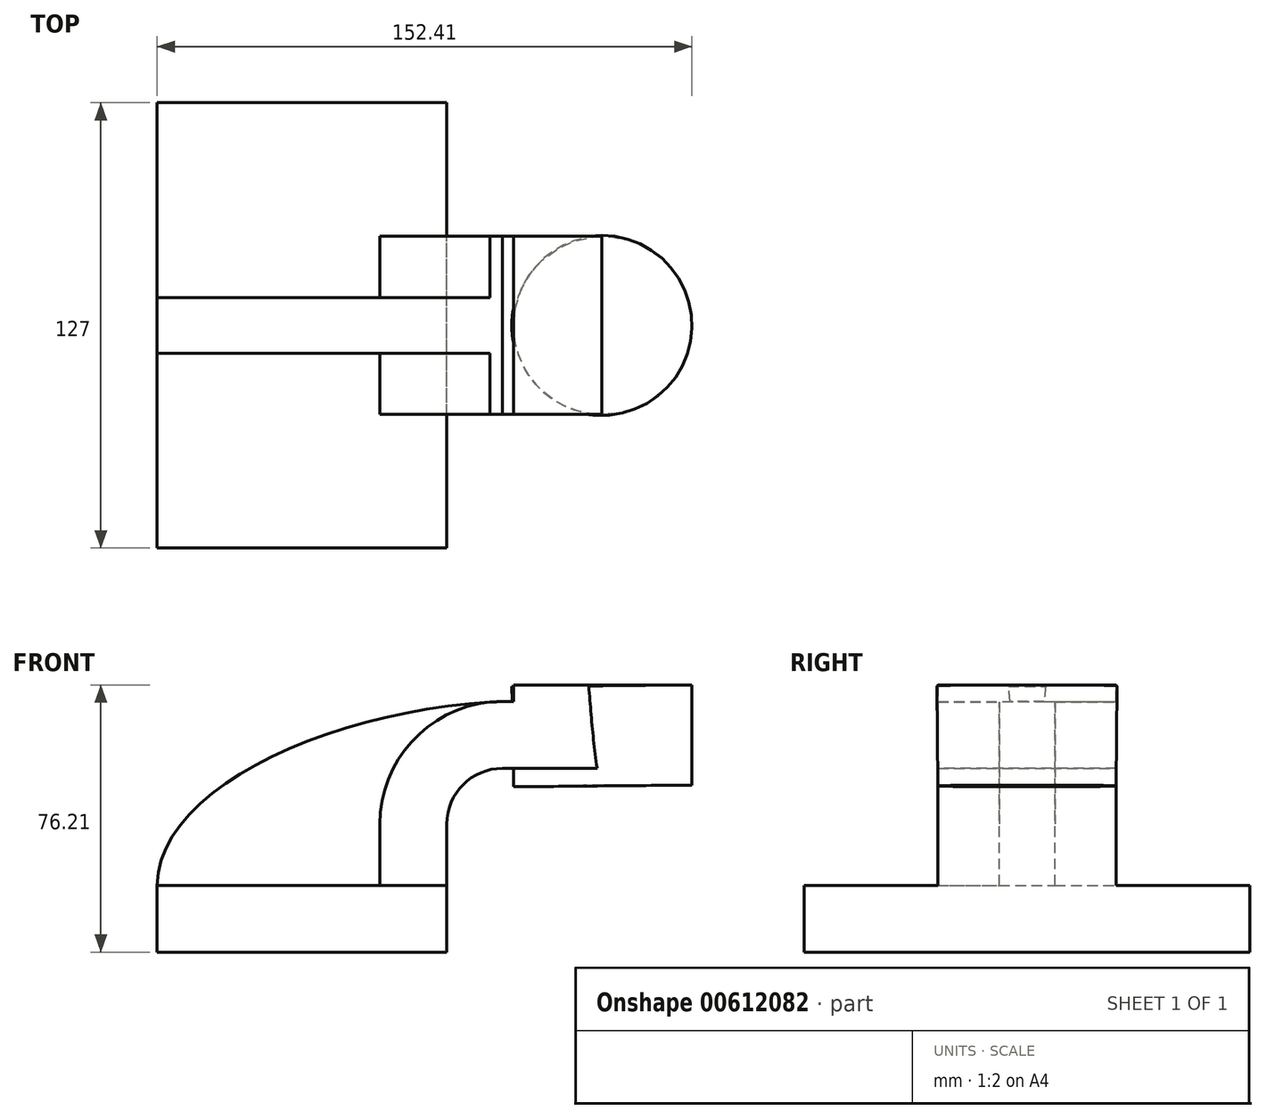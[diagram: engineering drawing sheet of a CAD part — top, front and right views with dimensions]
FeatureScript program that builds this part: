
annotation { "Feature Type Name" : "Feature", "Feature Type Description" : "" }
export const myFeature = defineFeature(function(context is Context, id is Id, definition is map)
    precondition{}
    {
        {
            var Q0;
            Q0=qCreatedBy(makeId("Front.planeOp"),FACE);
            var sketch = newSketch(context, id + "F0", { "sketchPlane" : qUnion([Q0])});
            skLineSegment(sketch, "E0.bottom", {"start": v(-41.28, 9.52) * mm, "end": v(41.28, 9.53) * mm});
            skLineSegment(sketch, "E0.top", {"start": v(-41.28, -9.53) * mm, "end": v(41.28, -9.53) * mm});
            skLineSegment(sketch, "E0.left", {"start": v(-41.28, 9.52) * mm, "end": v(-41.28, -9.53) * mm});
            skLineSegment(sketch, "E0.right", {"start": v(41.28, 9.53) * mm, "end": v(41.28, -9.52) * mm});
            skPoint(sketch, "E0.middle", {"position": v(0, 0) * mm});
            skLineSegment(sketch, "E1.bottom", {"start": v(111.12, 38.1) * mm, "end": v(60.32, 38.1) * mm});
            skLineSegment(sketch, "E1.top", {"start": v(111.12, 66.68) * mm, "end": v(60.32, 66.68) * mm});
            skLineSegment(sketch, "E1.left", {"start": v(111.12, 38.1) * mm, "end": v(111.12, 66.68) * mm});
            skLineSegment(sketch, "E1.right", {"start": v(60.32, 38.1) * mm, "end": v(60.32, 66.68) * mm});
            skPoint(sketch, "E1.middle", {"position": v(85.72, 52.39) * mm});
            skLineSegment(sketch, "E2", {"start": v(41.27, 9.53) * mm, "end": v(41.27, 27) * mm});
            skArc(sketch, "E3", {"start": v(57.15, 42.88) * mm, "mid": v(45.92, 38.23) * mm, "end": v(41.27, 27) * mm});
            skLineSegment(sketch, "E4", {"start": v(57.15, 42.88) * mm, "end": v(85.83, 42.88) * mm});
            skLineSegment(sketch, "E5.0", {"start": v(57.15, 61.93) * mm, "end": v(85.45, 61.93) * mm});
            skArc(sketch, "E5.1", {"start": v(57.15, 61.93) * mm, "mid": v(32.45, 51.7) * mm, "end": v(22.22, 27) * mm});
            skLineSegment(sketch, "E5.2", {"start": v(22.22, 9.53) * mm, "end": v(22.22, 27) * mm});
            skPoint(sketch, "E6.startSnap0", {"position": v(85.72, 38.1) * mm});
            skLineSegment(sketch, "E7", {"start": v(85.72, 38.1) * mm, "end": v(85.45, 66.68) * mm});
            skFitSpline(sketch, "E8", {"points": [v(-41.28, 9.52) * mm, v(57.15, 61.93) * mm], "startDerivative": vector(0.9, 85.64) * mm, "endDerivative": vector(141.08, 5.7) * mm});
            skSolve(sketch);
        }
        {
            var Q0;
            Q0=makeQuery(id+"F0.imprint","IMPRINT",FACE,{"disambiguationData":[TD([[makeQuery(id+"F0.imprint","IMPRINT",EDGE,{"derivedFrom":sQuery(id+"F0.wireOp",EDGE,"E0.top")}),1.0]])]});
            extrude(context, id + "F1", {"entities" : qUnion([Q0]), "endBound" : BoundingType.SYMMETRIC, "depth" : 127 * mm, "offsetDistance" : 25.4 * mm});
        }
        {
            var Q0;
            {var subQ1=sQuery(id+"F0.wireOp",EDGE,"E2");Q0=makeQuery(id+"F0.imprint","IMPRINT",FACE,{"disambiguationData":[TD([[makeQuery(id+"F0.imprint","IMPRINT",EDGE,{"derivedFrom":subQ1}),1.0]])]});}
            var Q1;
            {var subQ0=sQuery(id+"F0.wireOp",EDGE,"E1.right");var subQ1=sQuery(id+"F0.wireOp",EDGE,"E1.top");var subQ2=makeQuery(id+"F0.imprint","INTERSECT",VERTEX,{"derivedFrom":[subQ1,subQ0]});Q1=makeQuery(id+"F0.imprint","IMPRINT",FACE,{"disambiguationData":[TD([[makeQuery(id+"F0.imprint","IMPRINT",EDGE,{"disambiguationData":[TD([[subQ2,1.0]])],"derivedFrom":subQ1}),1.0]])]});}
            extrude(context, id + "F2", {"entities" : qUnion([Q0, Q1]), "operationType" : NewBodyOperationType.ADD, "endBound" : BoundingType.SYMMETRIC, "depth" : 50.8 * mm, "offsetDistance" : 25.4 * mm});
        }
        {
            var Q0;
            {var subQ3=sQuery(id+"F0.wireOp",EDGE,"E5.2");Q0=makeQuery(id+"F0.imprint","IMPRINT",FACE,{"disambiguationData":[TD([[makeQuery(id+"F0.imprint","IMPRINT",EDGE,{"derivedFrom":subQ3}),1.0]])]});}
            extrude(context, id + "F3", {"entities" : qUnion([Q0]), "operationType" : NewBodyOperationType.ADD, "endBound" : BoundingType.SYMMETRIC, "depth" : 15.88 * mm, "offsetDistance" : 25.4 * mm});
        }
        {
            var Q0;
            {var subQ4=sQuery(id+"F0.wireOp",EDGE,"E1.left");Q0=makeQuery(id+"F0.imprint","IMPRINT",FACE,{"disambiguationData":[TD([[makeQuery(id+"F0.imprint","IMPRINT",EDGE,{"derivedFrom":subQ4}),1.0]])]});}
            var Q1;
            Q1=sQuery(id+"F0.wireOp",EDGE,"E7");
            revolve(context, id + "F4", {"operationType" : NewBodyOperationType.ADD, "entities" : qUnion([Q0]), "axis" : qUnion([Q1]), "revolveType" : RevolveType.FULL});
        }
    });
